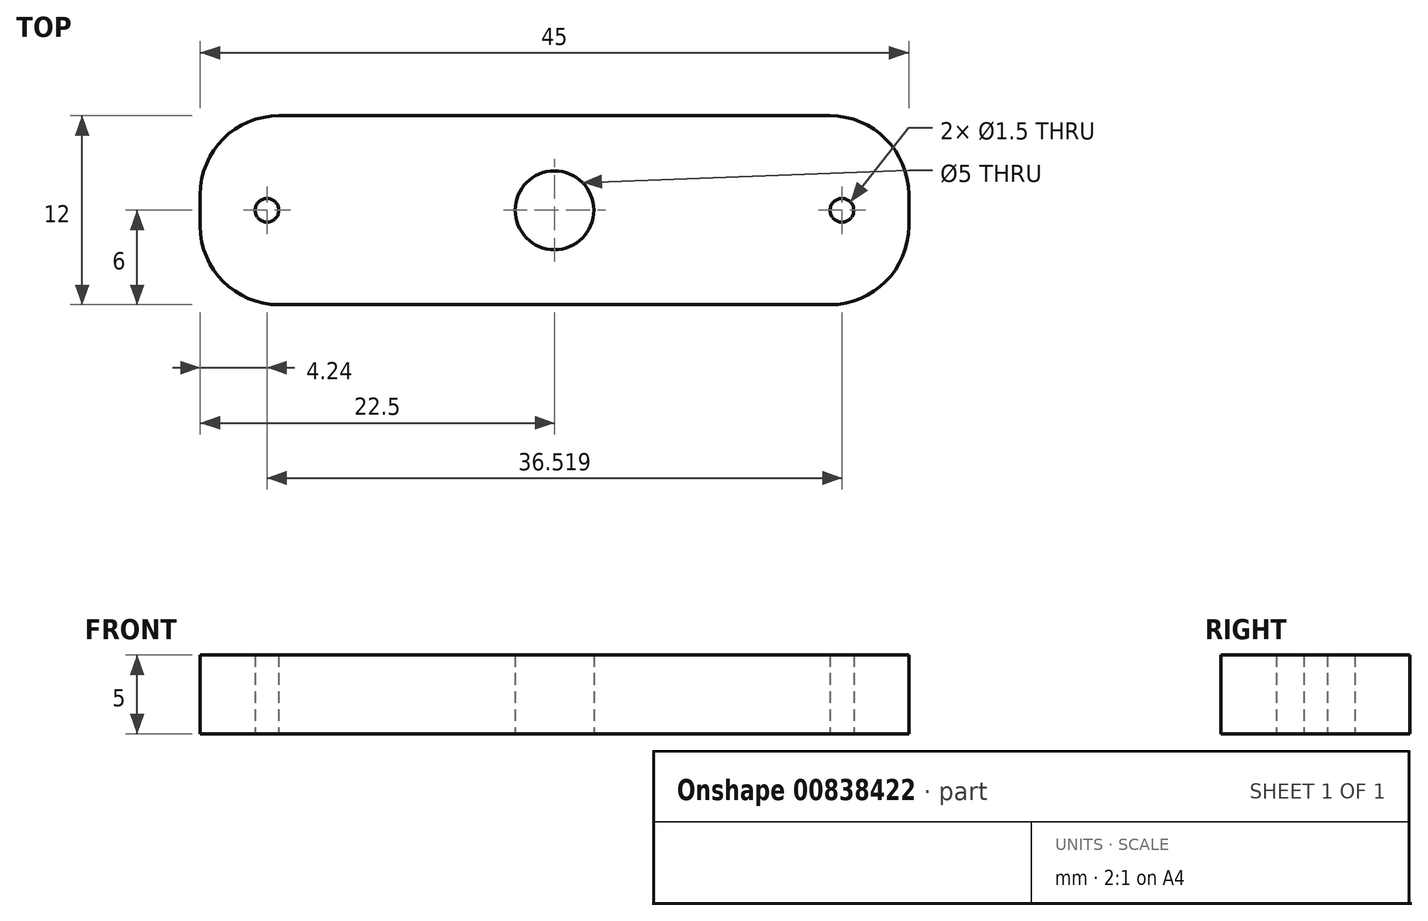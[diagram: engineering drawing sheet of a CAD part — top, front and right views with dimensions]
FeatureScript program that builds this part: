
annotation { "Feature Type Name" : "Feature", "Feature Type Description" : "" }
export const myFeature = defineFeature(function(context is Context, id is Id, definition is map)
    precondition{}
    {
        {
            var Q0;
            Q0=qCreatedBy(makeId("Top.planeOp"),FACE);
            var sketch = newSketch(context, id + "F0", { "sketchPlane" : qUnion([Q0])});
            skLineSegment(sketch, "E0.bottom", {"start": v(17.5, -6) * mm, "end": v(-17.5, -6) * mm});
            skLineSegment(sketch, "E0.top", {"start": v(17.5, 6) * mm, "end": v(-17.5, 6) * mm});
            skLineSegment(sketch, "E0.left", {"start": v(22.5, -1) * mm, "end": v(22.5, 1) * mm});
            skLineSegment(sketch, "E0.right", {"start": v(-22.5, -1) * mm, "end": v(-22.5, 1) * mm});
            skCircle(sketch, "E1", {"center": v(-18.26, 0) * mm, "radius": 0.75 * mm});
            skPoint(sketch, "E1.centerSnap0", {"position": v(-22.5, 0) * mm});
            skCircle(sketch, "E2.MirrorC", {"center": v(18.26, 0) * mm, "radius": 0.75 * mm});
            skCircle(sketch, "E3", {"center": v(0, 0) * mm, "radius": 2.5 * mm});
            skArc(sketch, "E4.filletArc", {"start": v(-17.5, 6) * mm, "mid": v(-21.04, 4.54) * mm, "end": v(-22.5, 1) * mm});
            skArc(sketch, "E5.filletArc", {"start": v(22.5, 1) * mm, "mid": v(21.04, 4.54) * mm, "end": v(17.5, 6) * mm});
            skArc(sketch, "E6.filletArc", {"start": v(17.5, -6) * mm, "mid": v(21.04, -4.54) * mm, "end": v(22.5, -1) * mm});
            skArc(sketch, "E7.filletArc", {"start": v(-22.5, -1) * mm, "mid": v(-21.04, -4.54) * mm, "end": v(-17.5, -6) * mm});
            skSolve(sketch);
        }
        {
            var Q0;
            Q0 = qSketchRegion(id + "F0", true);
            extrude(context, id + "F1", {"entities" : qUnion([Q0]), "depth" : 5 * mm, "offsetDistance" : 25 * mm});
        }
    });
